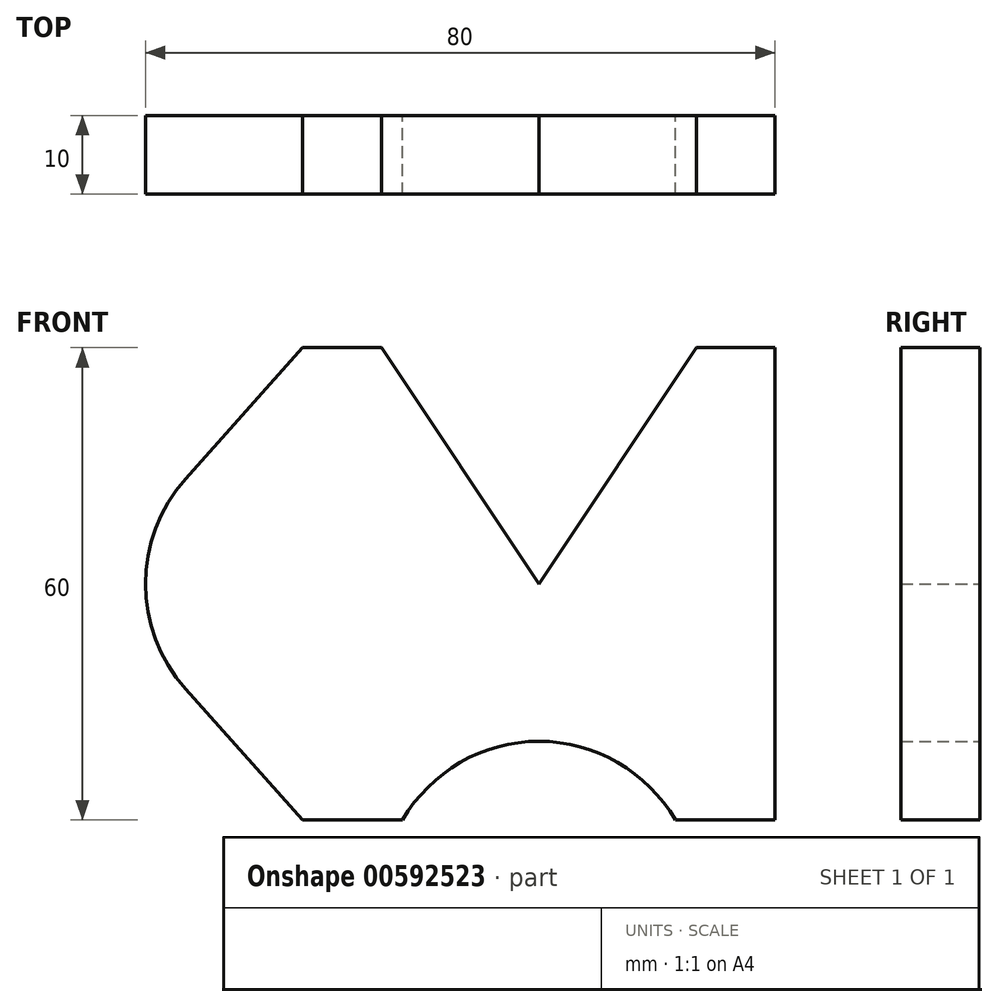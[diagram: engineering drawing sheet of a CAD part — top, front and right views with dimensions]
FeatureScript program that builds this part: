
annotation { "Feature Type Name" : "Feature", "Feature Type Description" : "" }
export const myFeature = defineFeature(function(context is Context, id is Id, definition is map)
    precondition{}
    {
        {
            var Q0;
            Q0=qCreatedBy(makeId("Front.planeOp"),FACE);
            var sketch = newSketch(context, id + "F0", { "sketchPlane" : qUnion([Q0])});
            skLineSegment(sketch, "E0", {"start": v(-20, 30) * mm, "end": v(0, 0) * mm});
            skLineSegment(sketch, "E1", {"start": v(0, 0) * mm, "end": v(20, 30) * mm});
            skLineSegment(sketch, "E2", {"start": v(20, 30) * mm, "end": v(30, 30) * mm});
            skLineSegment(sketch, "E3", {"start": v(30, 30) * mm, "end": v(30, -30) * mm});
            skLineSegment(sketch, "E4", {"start": v(30, -30) * mm, "end": v(17.32, -30) * mm});
            skLineSegment(sketch, "E5", {"start": v(-20, 30) * mm, "end": v(-30, 30) * mm});
            skLineSegment(sketch, "E6", {"start": v(-30, 30) * mm, "end": v(-44.9, 13.33) * mm});
            skLineSegment(sketch, "E7", {"start": v(-17.32, -30) * mm, "end": v(-30, -30) * mm});
            skLineSegment(sketch, "E8", {"start": v(-30, -30) * mm, "end": v(-44.9, -13.33) * mm});
            skArc(sketch, "E9", {"start": v(-44.9, 13.33) * mm, "mid": v(-50, 0) * mm, "end": v(-44.9, -13.33) * mm});
            skLineSegment(sketch, "E10", {"start": v(-30, 30) * mm, "end": v(-30, -30) * mm, "construction": true});
            skArc(sketch, "E11", {"start": v(17.32, -30) * mm, "mid": v(0, -20) * mm, "end": v(-17.32, -30) * mm});
            skSolve(sketch);
        }
        {
            var Q0;
            Q0=makeQuery(id+"F0.imprint","IMPRINT",FACE,{"disambiguationData":[TD([[makeQuery(id+"F0.imprint","IMPRINT",EDGE,{"derivedFrom":sQuery(id+"F0.wireOp",EDGE,"E0")}),-1.0]])]});
            extrude(context, id + "F1", {"entities" : qUnion([Q0]), "depth" : 10 * mm, "offsetDistance" : 25 * mm});
        }
    });
